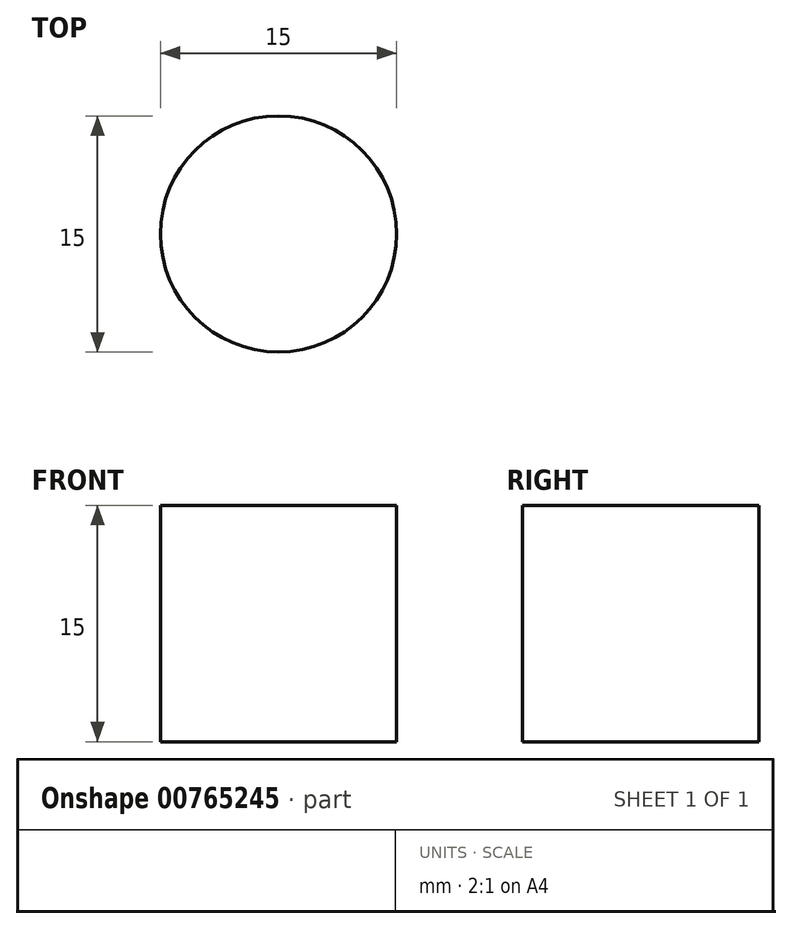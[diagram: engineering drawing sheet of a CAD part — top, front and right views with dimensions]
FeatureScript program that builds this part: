
annotation { "Feature Type Name" : "Feature", "Feature Type Description" : "" }
export const myFeature = defineFeature(function(context is Context, id is Id, definition is map)
    precondition{}
    {
        {
            var Q0;
            Q0=qCreatedBy(makeId("Top.planeOp"),FACE);
            var sketch = newSketch(context, id + "F0", { "sketchPlane" : qUnion([Q0])});
            skCircle(sketch, "E0", {"center": v(0, 0) * mm, "radius": 7.5 * mm});
            skSolve(sketch);
        }
        {
            var Q0;
            Q0 = qSketchRegion(id + "F0", true);
            extrude(context, id + "F1", {"entities" : qUnion([Q0]), "depth" : 15 * mm, "offsetDistance" : 25 * mm});
        }
    });
